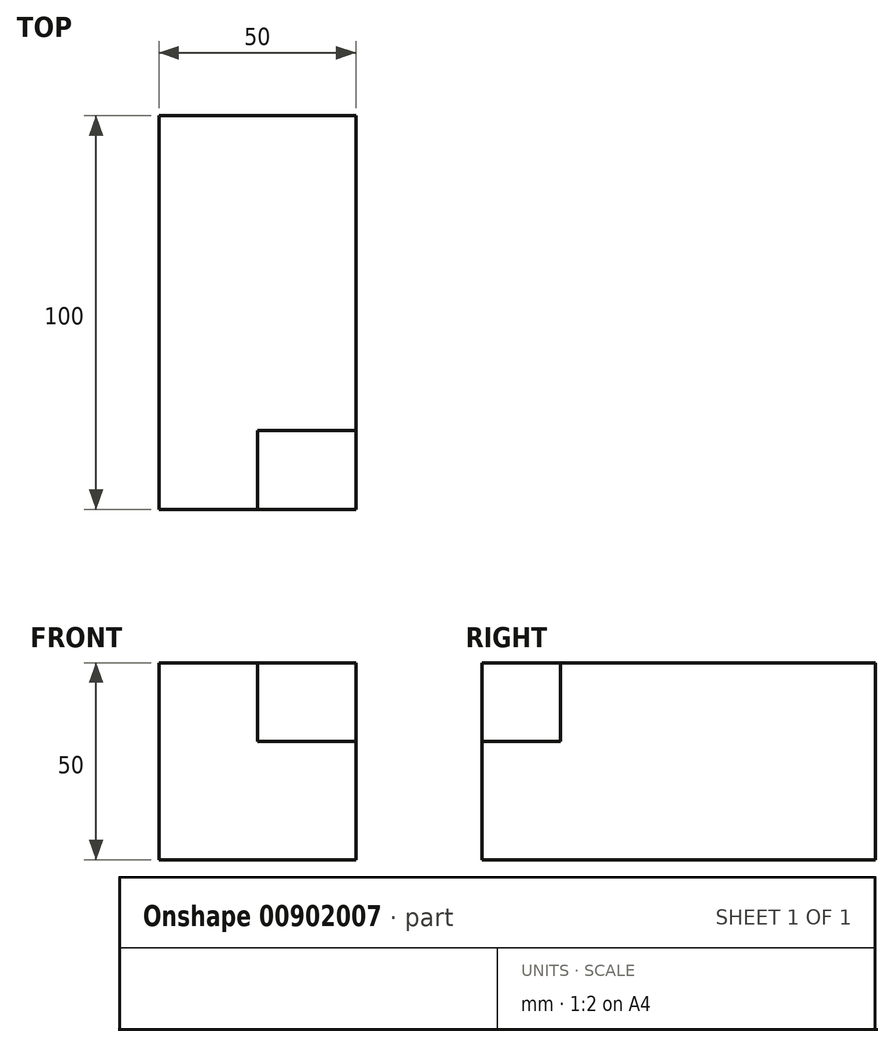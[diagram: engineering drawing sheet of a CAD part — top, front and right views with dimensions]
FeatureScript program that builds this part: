
annotation { "Feature Type Name" : "Feature", "Feature Type Description" : "" }
export const myFeature = defineFeature(function(context is Context, id is Id, definition is map)
    precondition{}
    {
        {
            var Q0;
            Q0=qCreatedBy(makeId("Front.planeOp"),FACE);
            var sketch = newSketch(context, id + "F0", { "sketchPlane" : qUnion([Q0])});
            skLineSegment(sketch, "E0.bottom", {"start": v(25, 25) * mm, "end": v(-25, 25) * mm});
            skLineSegment(sketch, "E0.top", {"start": v(25, -25) * mm, "end": v(-25, -25) * mm});
            skLineSegment(sketch, "E0.left", {"start": v(25, 25) * mm, "end": v(25, -25) * mm});
            skLineSegment(sketch, "E0.right", {"start": v(-25, 25) * mm, "end": v(-25, -25) * mm});
            skPoint(sketch, "E0.middle", {"position": v(0, 0) * mm});
            skSolve(sketch);
        }
        {
            var Q0;
            Q0=qSketchRegion(id+"F0",true);
            extrude(context, id + "F1", {"entities" : qUnion([Q0]), "endBound" : BoundingType.SYMMETRIC, "depth" : 100 * mm, "offsetDistance" : 25 * mm});
        }
        {
            var Q0;
            Q0=makeQuery(id+"F1.opExtrude","SWEPT_FACE",FACE,{"disambiguationData":[OSD([sQuery(id+"F0.wireOp",EDGE,"E0.left")])]});
            var sketch = newSketch(context, id + "F2", { "sketchPlane" : qUnion([Q0])});
            skLineSegment(sketch, "E1.bottom", {"start": v(-50, 25) * mm, "end": v(-30, 25) * mm});
            skLineSegment(sketch, "E1.top", {"start": v(-50, 5) * mm, "end": v(-30, 5) * mm});
            skLineSegment(sketch, "E1.left", {"start": v(-50, 25) * mm, "end": v(-50, 5) * mm});
            skLineSegment(sketch, "E1.right", {"start": v(-30, 25) * mm, "end": v(-30, 5) * mm});
            skSolve(sketch);
        }
        {
            var Q0;
            Q0=makeQuery(id+"F2.imprint","IMPRINT",FACE,{"disambiguationData":[TD([[makeQuery(id+"F2.imprint","IMPRINT",EDGE,{"derivedFrom":sQuery(id+"F2.wireOp",EDGE,"E1.bottom")}),-1.0]])]});
            extrude(context, id + "F3", {"entities" : qUnion([Q0]), "operationType" : NewBodyOperationType.REMOVE, "oppositeDirection" : true, "depth" : 25 * mm, "offsetDistance" : 25 * mm});
        }
    });
